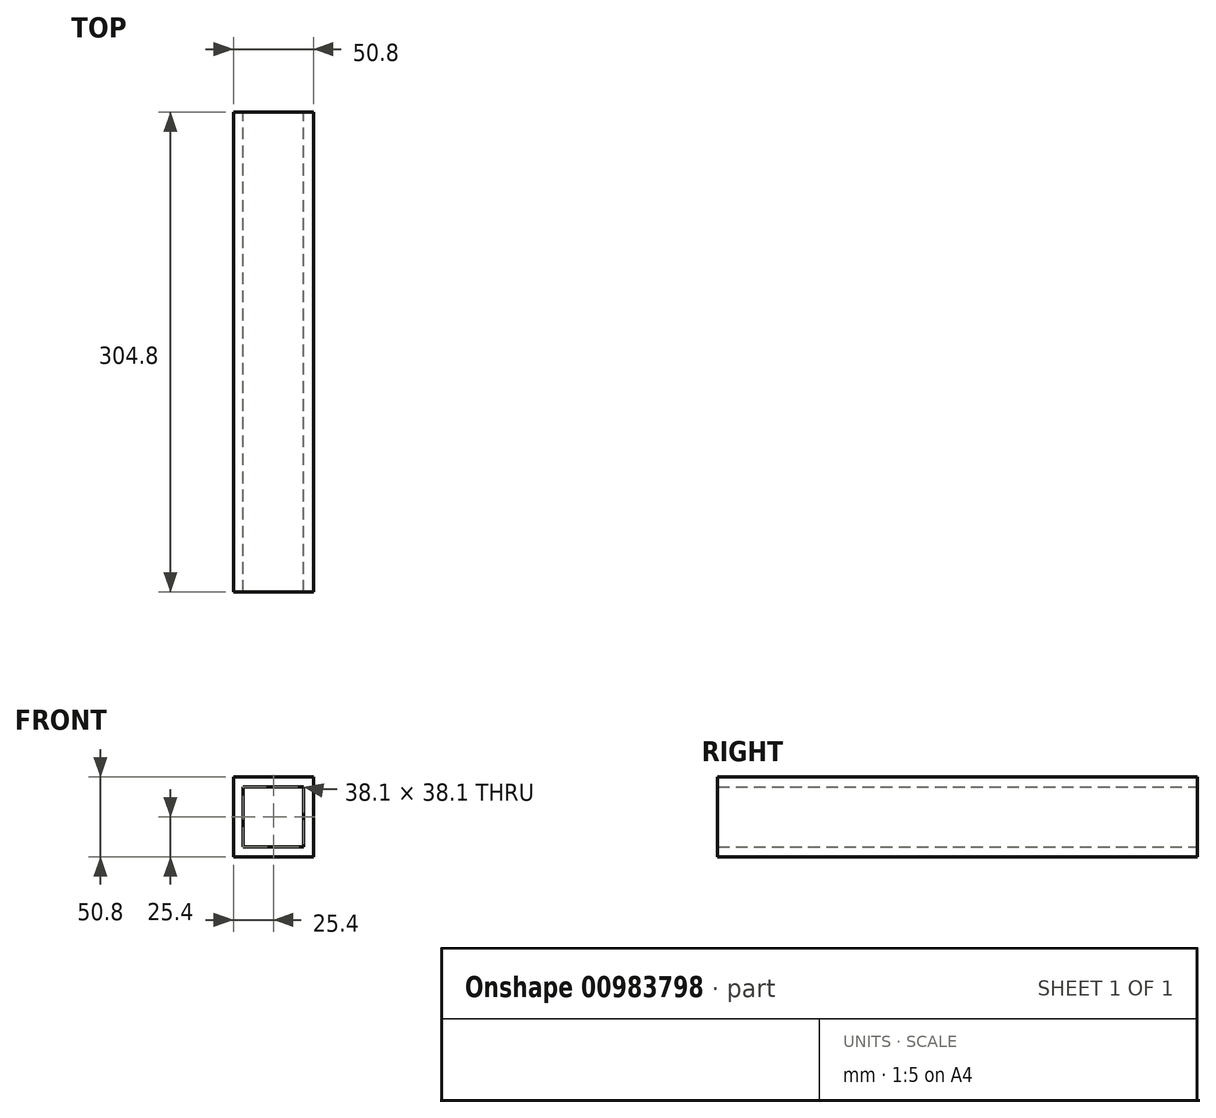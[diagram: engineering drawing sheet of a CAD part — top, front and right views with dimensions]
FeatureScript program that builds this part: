
annotation { "Feature Type Name" : "Feature", "Feature Type Description" : "" }
export const myFeature = defineFeature(function(context is Context, id is Id, definition is map)
    precondition{}
    {
        {
            var Q0;
            Q0=qCreatedBy(makeId("Front.planeOp"),FACE);
            var sketch = newSketch(context, id + "F0", { "sketchPlane" : qUnion([Q0])});
            skLineSegment(sketch, "E0.bottom", {"start": v(19.05, 19.05) * mm, "end": v(-19.05, 19.05) * mm});
            skLineSegment(sketch, "E0.top", {"start": v(19.05, -19.05) * mm, "end": v(-19.05, -19.05) * mm});
            skLineSegment(sketch, "E0.left", {"start": v(19.05, 19.05) * mm, "end": v(19.05, -19.05) * mm});
            skLineSegment(sketch, "E0.right", {"start": v(-19.05, 19.05) * mm, "end": v(-19.05, -19.05) * mm});
            skPoint(sketch, "E0.middle", {"position": v(0, 0) * mm});
            skLineSegment(sketch, "E1.bottom", {"start": v(25.4, 25.4) * mm, "end": v(-25.4, 25.4) * mm});
            skLineSegment(sketch, "E1.top", {"start": v(25.4, -25.4) * mm, "end": v(-25.4, -25.4) * mm});
            skLineSegment(sketch, "E1.left", {"start": v(25.4, 25.4) * mm, "end": v(25.4, -25.4) * mm});
            skLineSegment(sketch, "E1.right", {"start": v(-25.4, 25.4) * mm, "end": v(-25.4, -25.4) * mm});
            skSolve(sketch);
        }
        {
            var Q0;
            Q0 = qSketchRegion(id + "F0", true);
            extrude(context, id + "F1", {"entities" : qUnion([Q0]), "depth" : 304.8 * mm, "offsetDistance" : 25.4 * mm});
        }
    });
